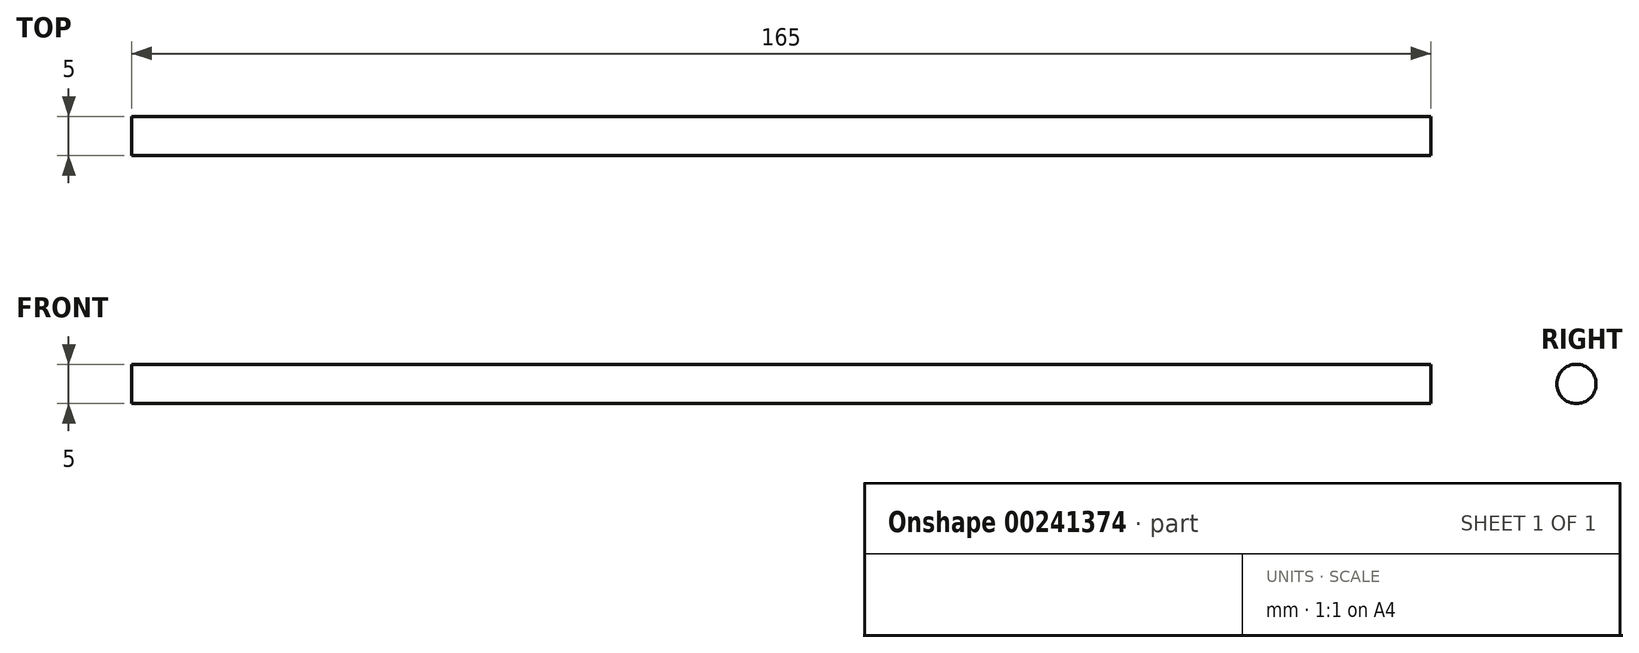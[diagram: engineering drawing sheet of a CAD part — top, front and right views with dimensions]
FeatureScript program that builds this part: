
annotation { "Feature Type Name" : "Feature", "Feature Type Description" : "" }
export const myFeature = defineFeature(function(context is Context, id is Id, definition is map)
    precondition{}
    {
        {
            var Q0;
            Q0=qCreatedBy(makeId("Right.planeOp"),FACE);
            var sketch = newSketch(context, id + "F0", { "sketchPlane" : qUnion([Q0])});
            skCircle(sketch, "E0", {"center": v(0, 0) * mm, "radius": 2.5 * mm});
            skSolve(sketch);
        }
        {
            var Q0;
            Q0 = qSketchRegion(id + "F0", true);
            extrude(context, id + "F1", {"entities" : qUnion([Q0]), "depth" : 165 * mm});
        }
    });
